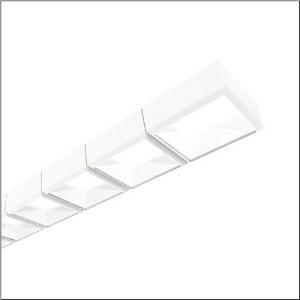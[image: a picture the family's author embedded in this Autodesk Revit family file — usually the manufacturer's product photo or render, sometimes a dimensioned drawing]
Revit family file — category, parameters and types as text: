
# Revit family: scriptus_11_5mz312d0twb
name_source: partatom
category: Lighting Fixtures
units: mm (PartAtom-declared; Revit-internal decimal feet)

## family parameters
Cut with Voids When Loaded = No
Host = Face
Light Source = No
Part Type = Normal
Room Calculation Point = No
Round Connector Dimension = Use Diameter
Shared = No

## types (1)
- --- (1 x LED 3000K+6500K / CRI = 80 (unbekannt), 3200 lm / 2380 lm, 3000K)
    Apparent Load = 94 VA
    CIE Flux Codes = 0 0 0 0 100 / 82 95 99 100 100
    Color Rendering = 80
    Color Temperature = 3000K
    Default Elevation = 1800 mm
    Description = Scriptus 11, office luminaire, primary optical cover: lenses, CAT 2 (L<= 3000cd/m²), light emission: direct/indirect distribution, primary light characteristic: symmetric, installation type: suspended mounting, LED, rated luminous flux: 11.150lm, luminous efficacy: 116lm/W, light colour: 8tw, colour temperature: 3000..6500K, control gear: DALI DT8, with terminal, 5-pole, mains connection: 230V, AC, 50Hz, rated input power: 96W, LED, control gear: ECG DALI, housing, luminaire housing, of aluminium, traffic white (RAL 9016), length: 1.768mm, width: 114mm, height: 57mm, protection rating (complete): IP20, insulation class (complete): insulation class I (protective earthing), certification: CE, protection symbol: F, permissible operating ambient temperature: <= +25°C, standard: EN 50419, packaging unit: 1 piece
    Height = 57 mm
    Lamp = 1 x LED 3000K+6500K / CRI >= 80 (unbekannt)
    Lamp Light Flux = 3200 lm / 2380 lm
    Lamp count = 1
    Length = 1768 mm
    Luminous efficacy = 119 lm/W
    Manufacturer = Siteco
    ModVariant = No
    Model = 5MZ312D0TWB
    Mounting Place = Ceiling
    Mounting Type = Pendant
    Number of Poles = 1
    OnlyDefault = Yes
    Power Factor = 1
    Product Name = Scriptus 11
    Product group = office luminaire | ceiling pendant
    ProductGroupID = 903
    Protection Class = Protection class I
    Protection Degree = IP 20
    RLX_Detail_Level = 1
    RLX_Emergency_Light_Flux = 0 lm
    RLX_Emergency_Type = 0
    RLX_Emergency_Type_DB = No
    RlxData = <blob elided: 31641 chars, md5=0dbceebd>
    Socket = socket
    Standby Power = 0 W
    System Light Flux = 11160 lm
    System Power = 94 W
    Type Comments = individual setting: colour temperature 6500K
    Type Image = l_1004839.jpg
    URL = http://relux.com
    VarID = @adj_196190
    Voltage = 0 V
    Weight = 0.00 kg
    Width = 114 mm

## geometry (parser evidence)
native form markers: Blend x4, Sweep x18
no freeform markers — native parametric forms only
